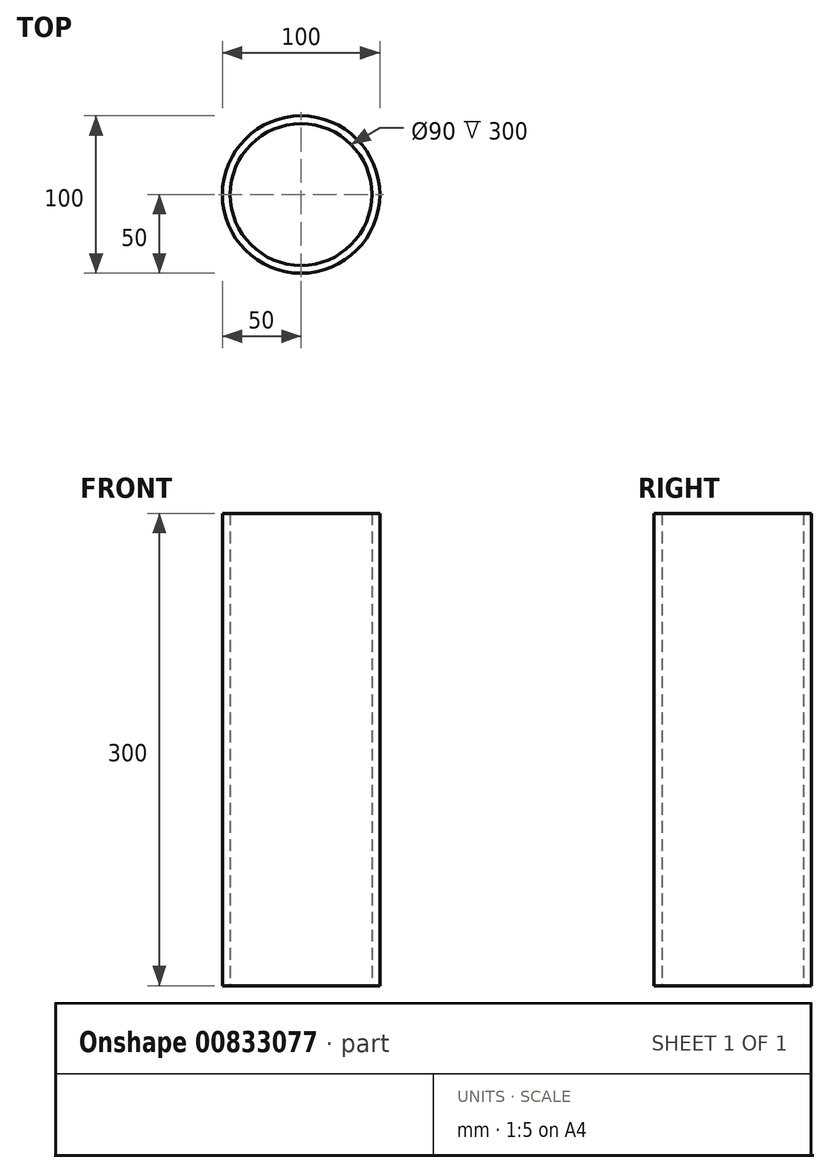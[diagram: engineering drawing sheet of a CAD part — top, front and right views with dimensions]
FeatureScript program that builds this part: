
annotation { "Feature Type Name" : "Feature", "Feature Type Description" : "" }
export const myFeature = defineFeature(function(context is Context, id is Id, definition is map)
    precondition{}
    {
        {
            var Q0;
            Q0=qCreatedBy(makeId("Top.planeOp"),FACE);
            var sketch = newSketch(context, id + "F0", { "sketchPlane" : qUnion([Q0])});
            skCircle(sketch, "E0", {"center": v(0, 0) * mm, "radius": 50 * mm});
            skCircle(sketch, "E1", {"center": v(0, 0) * mm, "radius": 45 * mm});
            skSolve(sketch);
        }
        {
            var Q0;
            Q0=makeQuery(id+"F0.imprint","IMPRINT",FACE,{"disambiguationData":[TD([[makeQuery(id+"F0.imprint","IMPRINT",EDGE,{"derivedFrom":sQuery(id+"F0.wireOp",EDGE,"E0")}),1.0]])]});
            extrude(context, id + "F1", {"entities" : qUnion([Q0]), "depth" : 300 * mm, "offsetDistance" : 25 * mm});
        }
        {
            var Q0;
            Q0=qCreatedBy(makeId("Right.planeOp"),FACE);
            cPlane(context, id + "F2", {"entities" : qUnion([Q0]), "cplaneType" : CPlaneType.OFFSET, "offset" : 50 * mm, "width" : 150 * mm, "height" : 150 * mm});
        }
    });
